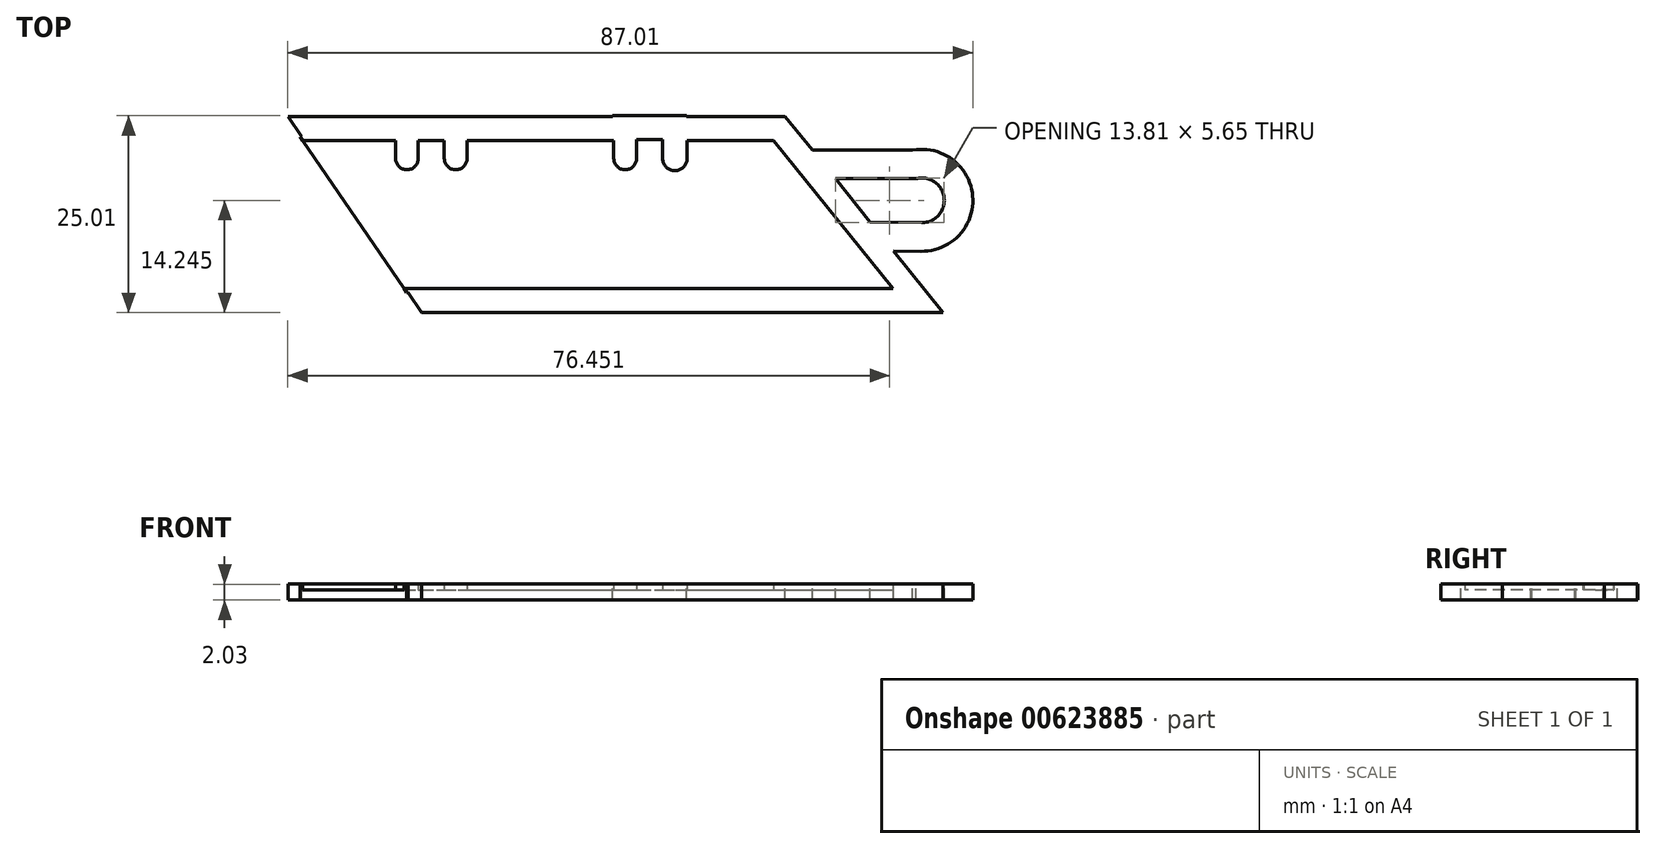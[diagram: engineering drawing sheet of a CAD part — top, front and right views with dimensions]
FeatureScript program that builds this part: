
annotation { "Feature Type Name" : "Feature", "Feature Type Description" : "" }
export const myFeature = defineFeature(function(context is Context, id is Id, definition is map)
    precondition{}
    {
        {
            var Q0;
            Q0=qCreatedBy(makeId("Top.planeOp"),FACE);
            var sketch = newSketch(context, id + "F0", { "sketchPlane" : qUnion([Q0])});
            skLineSegment(sketch, "E0.1", {"start": v(-13.86, 19.22) * mm, "end": v(-13.69, 19.22) * mm});
            skLineSegment(sketch, "E0.2", {"start": v(-13.86, 19.22) * mm, "end": v(-0.34, -0.63) * mm});
            skLineSegment(sketch, "E0.3", {"start": v(-0.34, -0.63) * mm, "end": v(-0.16, -0.63) * mm});
            skPoint(sketch, "E1.end.orphan", {"position": v(25.86, 16.42) * mm});
            skPoint(sketch, "E2.start.orphan", {"position": v(29, 16.42) * mm});
            skPoint(sketch, "E3.trimOffspring.start.orphan", {"position": v(29, 18.66) * mm});
            skPoint(sketch, "E4.end.orphan", {"position": v(32.05, 18.66) * mm});
            skPoint(sketch, "E5.start.orphan", {"position": v(32.05, 16.42) * mm});
            skPoint(sketch, "E6.end.orphan", {"position": v(35.43, 16.42) * mm});
            skPoint(sketch, "E7.start.orphan", {"position": v(-1.87, 16.42) * mm});
            skPoint(sketch, "E8.start.orphan", {"position": v(1.28, 16.42) * mm});
            skPoint(sketch, "E9.trimOffspring.start.orphan", {"position": v(1.28, 18.59) * mm});
            skPoint(sketch, "E10.end.orphan", {"position": v(4.33, 18.59) * mm});
            skPoint(sketch, "E11.start.orphan", {"position": v(4.33, 16.42) * mm});
            skPoint(sketch, "E12.end.orphan", {"position": v(7.48, 16.42) * mm});
            skLineSegment(sketch, "E13.0", {"start": v(-1.9, 21.76) * mm, "end": v(4.3, 21.76) * mm});
            skLineSegment(sketch, "E13.1", {"start": v(-15.42, 21.76) * mm, "end": v(-1.9, 21.76) * mm});
            skLineSegment(sketch, "E13.2", {"start": v(4.3, 21.76) * mm, "end": v(25.83, 21.76) * mm});
            skLineSegment(sketch, "E13.4", {"start": v(1.57, -3.17) * mm, "end": v(67.8, -3.17) * mm});
            skLineSegment(sketch, "E13.5", {"start": v(47.75, 21.76) * mm, "end": v(50.49, 18.36) * mm});
            skLineSegment(sketch, "E13.6", {"start": v(25.83, 21.76) * mm, "end": v(25.83, 21.84) * mm});
            skLineSegment(sketch, "E13.7", {"start": v(25.83, 21.84) * mm, "end": v(35.23, 21.84) * mm});
            skLineSegment(sketch, "E13.8", {"start": v(35.23, 21.76) * mm, "end": v(35.23, 21.84) * mm});
            skLineSegment(sketch, "E13.9", {"start": v(35.23, 21.76) * mm, "end": v(47.75, 21.76) * mm});
            skLineSegment(sketch, "E14", {"start": v(-15.42, 21.76) * mm, "end": v(-13.69, 19.22) * mm});
            skLineSegment(sketch, "E15.trimOffspring", {"start": v(-0.16, -0.63) * mm, "end": v(1.57, -3.17) * mm});
            skLineSegment(sketch, "E16", {"start": v(50.49, 18.36) * mm, "end": v(51.2, 17.46) * mm});
            skArc(sketch, "E17", {"start": v(65, 4.62) * mm, "mid": v(71.57, 11.62) * mm, "end": v(63.96, 17.46) * mm});
            skLineSegment(sketch, "E18", {"start": v(63.96, 17.46) * mm, "end": v(51.2, 17.46) * mm});
            skLineSegment(sketch, "E19", {"start": v(65, 4.62) * mm, "end": v(61.48, 4.68) * mm});
            skLineSegment(sketch, "E20.0", {"start": v(64.35, 13.83) * mm, "end": v(54.13, 13.83) * mm});
            skArc(sketch, "E20.1", {"start": v(65.07, 8.25) * mm, "mid": v(67.94, 11.45) * mm, "end": v(64.35, 13.83) * mm});
            skLineSegment(sketch, "E20.2", {"start": v(65.07, 8.25) * mm, "end": v(61.55, 8.31) * mm});
            skLineSegment(sketch, "E21.trimOffspring", {"start": v(54.13, 13.83) * mm, "end": v(58.52, 8.37) * mm});
            skLineSegment(sketch, "E22", {"start": v(62.34, 8.3) * mm, "end": v(58.52, 8.37) * mm});
            skLineSegment(sketch, "E23.trimOffspring", {"start": v(61.48, 4.68) * mm, "end": v(67.8, -3.17) * mm});
            skLineSegment(sketch, "E24.0", {"start": v(0.27, -0.13) * mm, "end": v(61.44, -0.13) * mm});
            skLineSegment(sketch, "E24.1", {"start": v(46.29, 18.71) * mm, "end": v(61.44, -0.13) * mm});
            skLineSegment(sketch, "E24.2", {"start": v(35.3, 18.71) * mm, "end": v(46.29, 18.71) * mm});
            skLineSegment(sketch, "E24.3", {"start": v(35.3, 18.71) * mm, "end": v(35.3, 16.42) * mm});
            skArc(sketch, "E24.4", {"start": v(32.18, 16.42) * mm, "mid": v(33.74, 14.86) * mm, "end": v(35.3, 16.42) * mm});
            skLineSegment(sketch, "E24.5", {"start": v(32.18, 16.42) * mm, "end": v(32.18, 18.8) * mm});
            skLineSegment(sketch, "E24.6", {"start": v(28.88, 18.8) * mm, "end": v(32.18, 18.8) * mm});
            skLineSegment(sketch, "E24.7", {"start": v(28.88, 16.42) * mm, "end": v(28.88, 18.8) * mm});
            skArc(sketch, "E24.8", {"start": v(25.98, 16.42) * mm, "mid": v(27.43, 14.97) * mm, "end": v(28.88, 16.42) * mm});
            skLineSegment(sketch, "E24.9", {"start": v(1.16, 16.42) * mm, "end": v(1.16, 18.71) * mm});
            skArc(sketch, "E24.10", {"start": v(-1.74, 16.42) * mm, "mid": v(-0.3, 14.97) * mm, "end": v(1.16, 16.42) * mm});
            skLineSegment(sketch, "E24.11", {"start": v(-1.74, 18.71) * mm, "end": v(-1.74, 16.42) * mm});
            skLineSegment(sketch, "E24.12", {"start": v(-13.52, 18.71) * mm, "end": v(-1.74, 18.71) * mm});
            skLineSegment(sketch, "E24.13", {"start": v(1.16, 18.71) * mm, "end": v(4.46, 18.71) * mm});
            skLineSegment(sketch, "E24.14", {"start": v(4.46, 16.42) * mm, "end": v(4.46, 18.71) * mm});
            skArc(sketch, "E24.15", {"start": v(4.46, 16.42) * mm, "mid": v(5.9, 14.97) * mm, "end": v(7.35, 16.42) * mm});
            skLineSegment(sketch, "E24.16", {"start": v(7.35, 18.71) * mm, "end": v(7.35, 16.42) * mm});
            skLineSegment(sketch, "E24.17", {"start": v(7.35, 18.71) * mm, "end": v(25.98, 18.71) * mm});
            skLineSegment(sketch, "E24.18", {"start": v(25.98, 18.71) * mm, "end": v(25.98, 16.42) * mm});
            skLineSegment(sketch, "E25", {"start": v(0.27, -0.13) * mm, "end": v(-0.68, -0.13) * mm});
            skSolve(sketch);
        }
        {
            var Q0;
            {var subQ4=sQuery(id+"F0.wireOp",EDGE,"E0.1");Q0=makeQuery(id+"F0.imprint","IMPRINT",FACE,{"disambiguationData":[TD([[makeQuery(id+"F0.imprint","IMPRINT",EDGE,{"derivedFrom":subQ4}),-1.0]])]});}
            var Q1;
            Q1=makeQuery(id+"F0.imprint","IMPRINT",FACE,{"disambiguationData":[TD([[makeQuery(id+"F0.imprint","IMPRINT",EDGE,{"derivedFrom":sQuery(id+"F0.wireOp",EDGE,"E24.0")}),1.0]])]});
            extrude(context, id + "F1", {"entities" : qUnion([Q0, Q1]), "oppositeDirection" : true, "depth" : 1.27 * mm, "offsetDistance" : 25.4 * mm});
        }
        {
            var Q0;
            {var subQ4=sQuery(id+"F0.wireOp",EDGE,"E0.1");Q0=makeQuery(id+"F0.imprint","IMPRINT",FACE,{"disambiguationData":[TD([[makeQuery(id+"F0.imprint","IMPRINT",EDGE,{"derivedFrom":subQ4}),-1.0]])]});}
            extrude(context, id + "F2", {"entities" : qUnion([Q0]), "operationType" : NewBodyOperationType.ADD, "depth" : 0.76 * mm, "offsetDistance" : 25.4 * mm});
        }
    });
